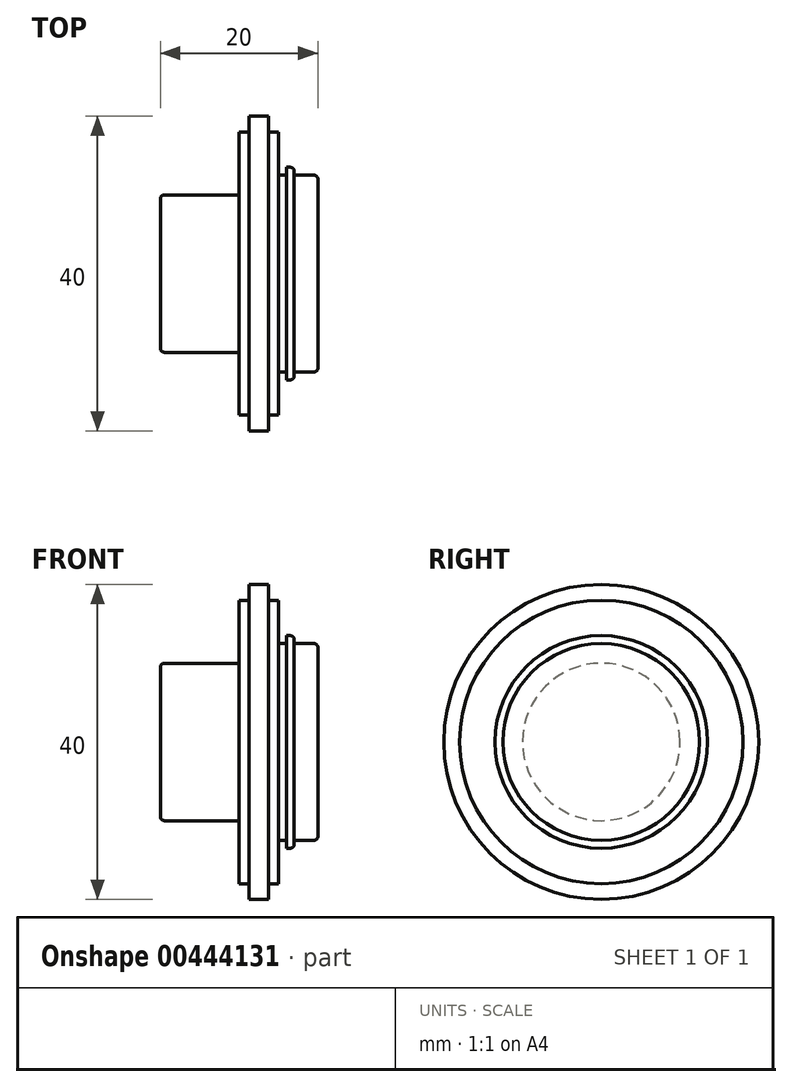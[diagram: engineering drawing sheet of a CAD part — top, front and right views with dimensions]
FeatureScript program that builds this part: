
annotation { "Feature Type Name" : "Feature", "Feature Type Description" : "" }
export const myFeature = defineFeature(function(context is Context, id is Id, definition is map)
    precondition{}
    {
        {
            var Q0;
            Q0=qCreatedBy(makeId("Front.planeOp"),FACE);
            var sketch = newSketch(context, id + "F0", { "sketchPlane" : qUnion([Q0])});
            skLineSegment(sketch, "E0", {"start": v(0, 0) * mm, "end": v(-20, 0) * mm});
            skLineSegment(sketch, "E1", {"start": v(-20, 0) * mm, "end": v(-20, 10) * mm});
            skLineSegment(sketch, "E2", {"start": v(-20, 10) * mm, "end": v(-10, 10) * mm});
            skLineSegment(sketch, "E3", {"start": v(-10, 10) * mm, "end": v(-10, 18) * mm});
            skLineSegment(sketch, "E4", {"start": v(-10, 18) * mm, "end": v(-8.75, 18) * mm});
            skLineSegment(sketch, "E5", {"start": v(-8.75, 18) * mm, "end": v(-8.75, 20) * mm});
            skLineSegment(sketch, "E6", {"start": v(-8.75, 20) * mm, "end": v(-6.25, 20) * mm});
            skLineSegment(sketch, "E7", {"start": v(-6.25, 20) * mm, "end": v(-6.25, 18) * mm});
            skLineSegment(sketch, "E8", {"start": v(-6.25, 18) * mm, "end": v(-5, 18) * mm});
            skLineSegment(sketch, "E9", {"start": v(-5, 18) * mm, "end": v(-5, 12.5) * mm});
            skLineSegment(sketch, "E10", {"start": v(-5, 12.5) * mm, "end": v(-4, 12.5) * mm});
            skLineSegment(sketch, "E11", {"start": v(-4, 12.5) * mm, "end": v(-4, 13.5) * mm});
            skLineSegment(sketch, "E12", {"start": v(-4, 13.5) * mm, "end": v(-3, 13.5) * mm});
            skLineSegment(sketch, "E13", {"start": v(-3, 13.5) * mm, "end": v(-3, 12.5) * mm});
            skLineSegment(sketch, "E14", {"start": v(-3, 12.5) * mm, "end": v(0, 12.5) * mm});
            skLineSegment(sketch, "E15", {"start": v(0, 12.5) * mm, "end": v(0, 0) * mm});
            skLineSegment(sketch, "E16", {"start": v(0, 0) * mm, "end": v(0, 0) * mm});
            skSolve(sketch);
        }
        {
            var Q0;
            Q0 = qSketchRegion(id + "F0", true);
            var Q1;
            Q1=sQuery(id+"F0.wireOp",EDGE,"E0");
            revolve(context, id + "F1", {"entities" : qUnion([Q0]), "axis" : qUnion([Q1]), "revolveType" : RevolveType.FULL});
        }
        {
            var Q0;
            Q0=makeQuery(id+"F1.opRevolve","SWEPT_EDGE",EDGE,{"disambiguationData":[OSD([sQuery(id+"F0.wireOp",EDGE,"E1"),sQuery(id+"F0.wireOp",EDGE,"E2")])]});
            var Q1;
            Q1=makeQuery(id+"F1.opRevolve","SWEPT_EDGE",EDGE,{"disambiguationData":[OSD([sQuery(id+"F0.wireOp",EDGE,"E12"),sQuery(id+"F0.wireOp",EDGE,"E13")])]});
            var Q2;
            Q2=makeQuery(id+"F1.opRevolve","SWEPT_EDGE",EDGE,{"disambiguationData":[OSD([sQuery(id+"F0.wireOp",EDGE,"E14"),sQuery(id+"F0.wireOp",EDGE,"E15")])]});
            fillet(context, id + "F2", {"entities" : qUnion([Q0, Q1, Q2]), "radius" : 0.5 * mm, "tangentPropagation" : true, "allowEdgeOverflow" : false});
        }
    });
